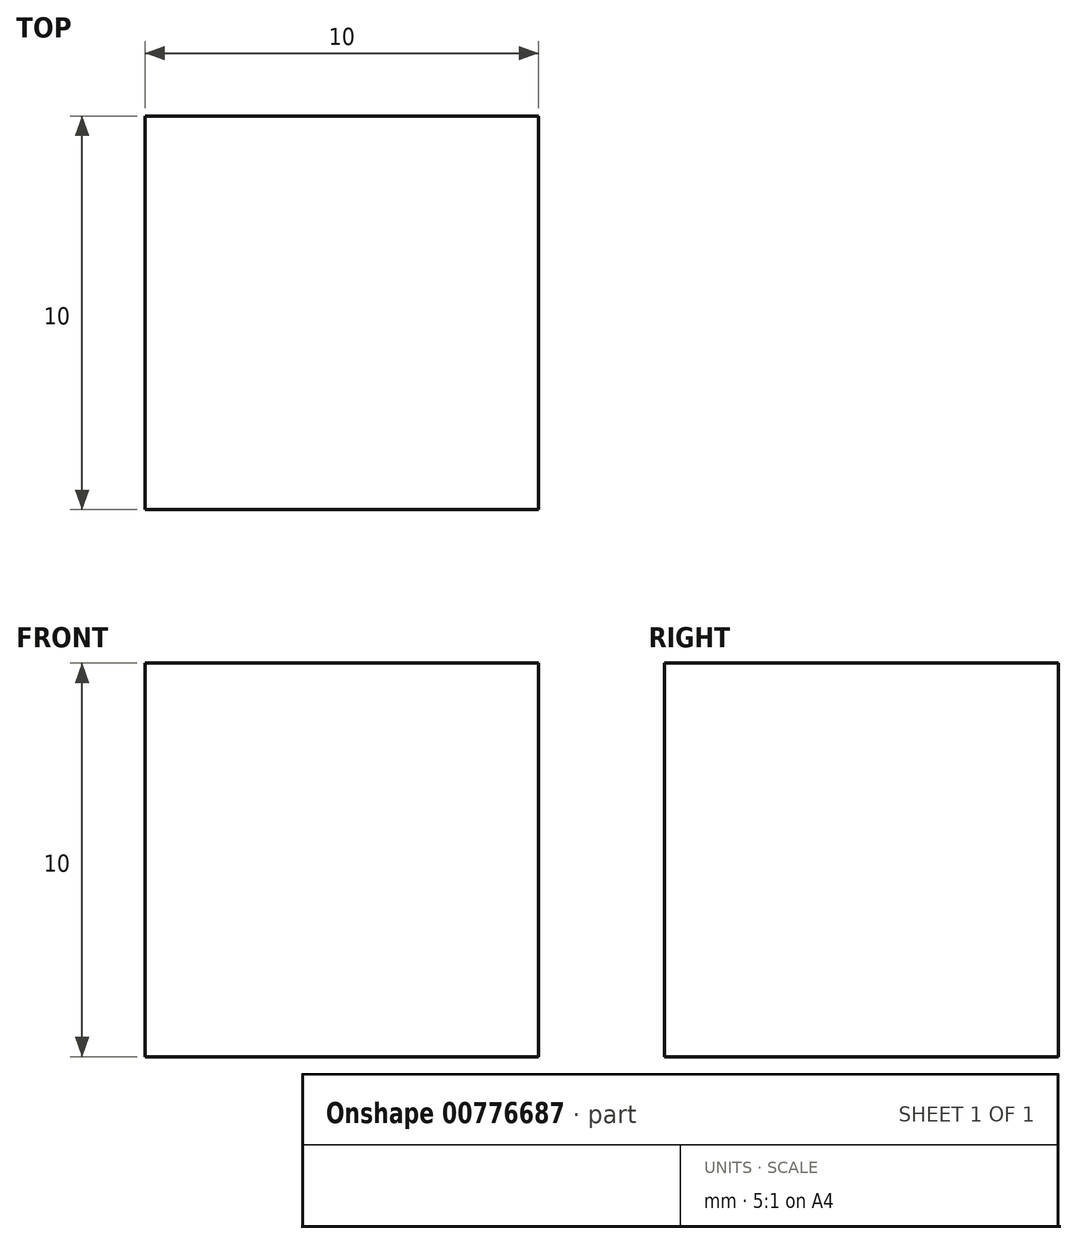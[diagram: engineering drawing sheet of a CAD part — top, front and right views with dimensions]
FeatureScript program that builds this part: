
annotation { "Feature Type Name" : "Feature", "Feature Type Description" : "" }
export const myFeature = defineFeature(function(context is Context, id is Id, definition is map)
    precondition{}
    {
        {
            var Q0;
            Q0=qCreatedBy(makeId("Top.planeOp"),FACE);
            var sketch = newSketch(context, id + "F0", { "sketchPlane" : qUnion([Q0])});
            skLineSegment(sketch, "E0.bottom", {"start": v(0, 0) * mm, "end": v(10, 0) * mm});
            skLineSegment(sketch, "E0.top", {"start": v(0, -10) * mm, "end": v(10, -10) * mm});
            skLineSegment(sketch, "E0.left", {"start": v(0, 0) * mm, "end": v(0, -10) * mm});
            skLineSegment(sketch, "E0.right", {"start": v(10, 0) * mm, "end": v(10, -10) * mm});
            skSolve(sketch);
        }
        {
            var Q0;
            Q0=makeQuery(id+"F0.imprint","IMPRINT",FACE,{"disambiguationData":[TD([[makeQuery(id+"F0.imprint","IMPRINT",EDGE,{"derivedFrom":sQuery(id+"F0.wireOp",EDGE,"E0.bottom")}),-1.0]])]});
            extrude(context, id + "F1", {"entities" : qUnion([Q0]), "depth" : 10 * mm, "offsetDistance" : 25 * mm});
        }
    });
